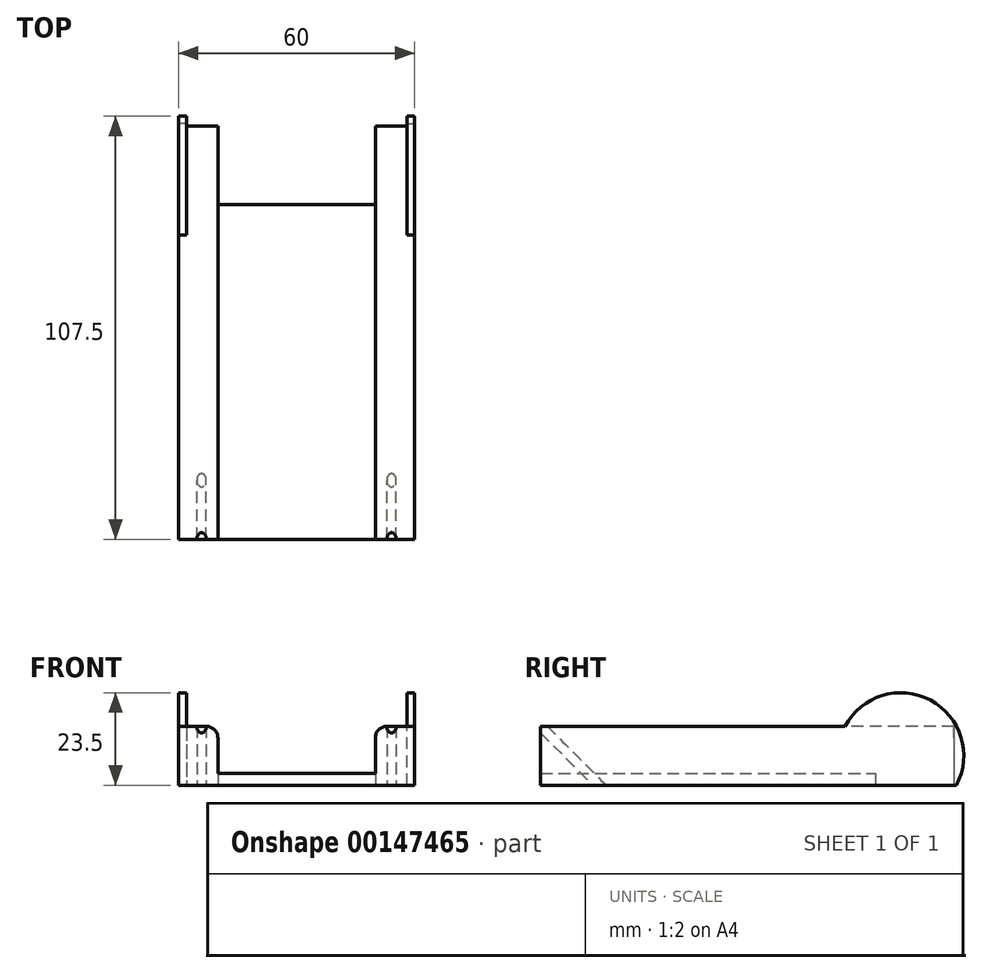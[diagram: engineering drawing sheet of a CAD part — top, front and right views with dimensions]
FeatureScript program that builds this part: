
annotation { "Feature Type Name" : "Feature", "Feature Type Description" : "" }
export const myFeature = defineFeature(function(context is Context, id is Id, definition is map)
    precondition{}
    {
        {
            var Q0;
            Q0=qCreatedBy(makeId("Top.planeOp"),FACE);
            var Q1;
            Q1=qCreatedBy(makeId("Front.planeOp"),FACE);
            cPlane(context, id + "F0", {"entities" : qUnion([Q0, Q1]), "cplaneType" : CPlaneType.MID_PLANE, "offset" : 25 * mm, "flipAlignment" : true, "width" : 150 * mm, "height" : 150 * mm});
        }
        {
            var Q0;
            Q0=qCreatedBy(id+"F0.planeOp",FACE);
            var sketch = newSketch(context, id + "F1", { "sketchPlane" : qUnion([Q0])});
            skLineSegment(sketch, "E0", {"start": v(-24.13, 0) * mm, "end": v(24.13, 0) * mm});
            skCircle(sketch, "E1", {"center": v(-24.13, 0) * mm, "radius": 1 * mm});
            skCircle(sketch, "E2", {"center": v(24.13, 0) * mm, "radius": 1 * mm});
            skLineSegment(sketch, "E3", {"start": v(0, 0) * mm, "end": v(0, -22) * mm});
            skSolve(sketch);
        }
        {
            var Q0;
            Q0 = qSketchRegion(id + "F1", true);
            extrude(context, id + "F2", {"entities" : qUnion([Q0]), "depth" : 100 * mm, "hasSecondDirection" : true, "secondDirectionOppositeDirection" : true, "secondDirectionDepth" : 20 * mm});
        }
        {
            var Q0;
            Q0=qCreatedBy(makeId("Front.planeOp"),FACE);
            var sketch = newSketch(context, id + "F3", { "sketchPlane" : qUnion([Q0])});
            skLineSegment(sketch, "E4.bottom", {"start": v(-30, 0) * mm, "end": v(30, 0) * mm});
            skLineSegment(sketch, "E4.top", {"start": v(-30, 15) * mm, "end": v(-23, 15) * mm});
            skLineSegment(sketch, "E4.left", {"start": v(-30, 0) * mm, "end": v(-30, 15) * mm});
            skLineSegment(sketch, "E4.right", {"start": v(30, 0) * mm, "end": v(30, 15) * mm});
            skPoint(sketch, "E4.middle", {"position": v(0, 7.5) * mm});
            skLineSegment(sketch, "E5.top", {"start": v(-20, 3) * mm, "end": v(20, 3) * mm});
            skLineSegment(sketch, "E5.left", {"start": v(-20, 12) * mm, "end": v(-20, 3) * mm});
            skLineSegment(sketch, "E5.right", {"start": v(20, 12) * mm, "end": v(20, 3) * mm});
            skPoint(sketch, "E5.middle", {"position": v(0, 9) * mm});
            skPoint(sketch, "E6.centerSnap0", {"position": v(0, 15) * mm});
            skLineSegment(sketch, "E7.trimOffspring", {"start": v(23, 15) * mm, "end": v(30, 15) * mm});
            skPoint(sketch, "E8.visualSharp", {"position": v(-20, 15) * mm});
            skArc(sketch, "E8.filletArc", {"start": v(-20, 12) * mm, "mid": v(-20.88, 14.12) * mm, "end": v(-23, 15) * mm});
            skPoint(sketch, "E9.visualSharp", {"position": v(20, 15) * mm});
            skArc(sketch, "E9.filletArc", {"start": v(23, 15) * mm, "mid": v(20.88, 14.12) * mm, "end": v(20, 12) * mm});
            skCircle(sketch, "E10", {"center": v(0, 28.66) * mm, "radius": 25.4 * mm, "construction": true});
            skSolve(sketch);
        }
        {
            var Q0;
            Q0=makeQuery(id+"F3.imprint","IMPRINT",FACE,{"disambiguationData":[TD([[makeQuery(id+"F3.imprint","IMPRINT",EDGE,{"derivedFrom":sQuery(id+"F3.wireOp",EDGE,"E4.bottom")}),1.0]])]});
            extrude(context, id + "F4", {"entities" : qUnion([Q0]), "depth" : 15 * mm, "hasSecondDirection" : true, "secondDirectionOppositeDirection" : true, "secondDirectionDepth" : 90 * mm});
        }
        {
            var Q0;
            Q0=qCreatedBy(makeId("Right.planeOp"),FACE);
            var sketch = newSketch(context, id + "F5", { "sketchPlane" : qUnion([Q0])});
            skPoint(sketch, "E11.0", {"position": v(-15, 15) * mm});
            skLineSegment(sketch, "E12", {"start": v(0, 0) * mm, "end": v(-15, 15) * mm});
            skLineSegment(sketch, "E13", {"start": v(-7.5, 7.5) * mm, "end": v(76.5, 7.5) * mm});
            skCircle(sketch, "E14", {"center": v(76.5, 7.5) * mm, "radius": 16 * mm});
            skSolve(sketch);
        }
        {
            var Q0;
            Q0=makeQuery(id+"F4.opExtrude","SWEPT_FACE",FACE,{"disambiguationData":[OSD([sQuery(id+"F3.wireOp",EDGE,"E4.left")])]});
            var sketch = newSketch(context, id + "F6", { "sketchPlane" : qUnion([Q0])});
            skCircle(sketch, "E15.0", {"center": v(-76.5, 7.5) * mm, "radius": 16 * mm});
            skSolve(sketch);
        }
        {
            var Q0;
            Q0 = qSketchRegion(id + "F6", true);
            extrude(context, id + "F7", {"entities" : qUnion([Q0]), "operationType" : NewBodyOperationType.ADD, "oppositeDirection" : true, "depth" : 2 * mm});
        }
        {
            var Q0;
            Q0=makeQuery(id+"F4.opExtrude","SWEPT_FACE",FACE,{"disambiguationData":[OSD([sQuery(id+"F3.wireOp",EDGE,"E4.right")])]});
            var sketch = newSketch(context, id + "F8", { "sketchPlane" : qUnion([Q0])});
            skCircle(sketch, "E16.0", {"center": v(76.5, 7.5) * mm, "radius": 16 * mm});
            skSolve(sketch);
        }
        {
            var Q0;
            Q0 = qSketchRegion(id + "F8", true);
            extrude(context, id + "F9", {"entities" : qUnion([Q0]), "operationType" : NewBodyOperationType.ADD, "oppositeDirection" : true, "depth" : 2 * mm});
        }
        {
            var Q0;
            Q0=qCreatedBy(makeId("Top.planeOp"),FACE);
            var sketch = newSketch(context, id + "F10", { "sketchPlane" : qUnion([Q0])});
            skPoint(sketch, "E17.0", {"position": v(-20, 90) * mm});
            skPoint(sketch, "E18.0", {"position": v(20, 90) * mm});
            skLineSegment(sketch, "E19.bottom", {"start": v(-20, 90) * mm, "end": v(20, 90) * mm});
            skLineSegment(sketch, "E19.top", {"start": v(-20, 70) * mm, "end": v(20, 70) * mm});
            skLineSegment(sketch, "E19.left", {"start": v(-20, 90) * mm, "end": v(-20, 70) * mm});
            skLineSegment(sketch, "E19.right", {"start": v(20, 90) * mm, "end": v(20, 70) * mm});
            skLineSegment(sketch, "E20", {"start": v(-30, 92.5) * mm, "end": v(-28, 92.5) * mm, "construction": true});
            skLineSegment(sketch, "E21.bottom", {"start": v(-28, 92.5) * mm, "end": v(-20, 92.5) * mm, "construction": true});
            skLineSegment(sketch, "E21.top", {"start": v(-28, 90) * mm, "end": v(-20, 90) * mm, "construction": true});
            skLineSegment(sketch, "E21.left", {"start": v(-28, 92.5) * mm, "end": v(-28, 90) * mm, "construction": true});
            skLineSegment(sketch, "E21.right", {"start": v(-20, 92.5) * mm, "end": v(-20, 90) * mm, "construction": true});
            skLineSegment(sketch, "E22", {"start": v(-30, 92.5) * mm, "end": v(-28, 92.5) * mm});
            skLineSegment(sketch, "E23.0", {"start": v(-28, 62.37) * mm, "end": v(-28, 92.5) * mm});
            skLineSegment(sketch, "E24", {"start": v(-28, 77.43) * mm, "end": v(-20, 77.43) * mm});
            skSolve(sketch);
        }
        {
            var Q0;
            Q0 = qSketchRegion(id + "F10", true);
            extrude(context, id + "F11", {"entities" : qUnion([Q0]), "operationType" : NewBodyOperationType.REMOVE, "depth" : 10 * mm});
        }
        {
            var Q0;
            Q0=qCreatedBy(id+"F0.planeOp",FACE);
            var sketch = newSketch(context, id + "F12", { "sketchPlane" : qUnion([Q0])});
            skLineSegment(sketch, "E25", {"start": v(-24.13, 0) * mm, "end": v(24.13, 0) * mm});
            skCircle(sketch, "E26", {"center": v(-24.13, 0) * mm, "radius": 1.2 * mm});
            skCircle(sketch, "E27", {"center": v(24.13, 0) * mm, "radius": 1.2 * mm});
            skSolve(sketch);
        }
        {
            var Q0;
            Q0 = qSketchRegion(id + "F12", true);
            extrude(context, id + "F13", {"entities" : qUnion([Q0]), "operationType" : NewBodyOperationType.REMOVE, "depth" : 124.25 * mm, "hasSecondDirection" : true, "secondDirectionOppositeDirection" : true, "secondDirectionDepth" : 109.5 * mm});
        }
        {
            var Q0;
            Q0=qCreatedBy(makeId("Right.planeOp"),FACE);
            var sketch = newSketch(context, id + "F14", { "sketchPlane" : qUnion([Q0])});
            skLineSegment(sketch, "E28.bottom", {"start": v(0, 0) * mm, "end": v(125.27, 0) * mm});
            skLineSegment(sketch, "E28.top", {"start": v(0, -20.9) * mm, "end": v(125.27, -20.9) * mm});
            skLineSegment(sketch, "E28.left", {"start": v(0, 0) * mm, "end": v(0, -20.9) * mm});
            skLineSegment(sketch, "E28.right", {"start": v(125.27, 0) * mm, "end": v(125.27, -20.9) * mm});
            skSolve(sketch);
        }
        {
            var Q0;
            Q0 = qSketchRegion(id + "F14", true);
            extrude(context, id + "F15", {"entities" : qUnion([Q0]), "operationType" : NewBodyOperationType.REMOVE, "endBound" : BoundingType.SYMMETRIC, "oppositeDirection" : true, "depth" : 80 * mm});
        }
    });
